# Revit family: IS_Connect_E8103_BIM_DE
name_source: partatom
category: Plumbing Fixtures
revit_build: Autodesk Revit MEP 2016 (Build: 20161004_0715(x64)
units: mm (PartAtom-declared; Revit-internal decimal feet)

## family parameters
Cut with Voids When Loaded = No
Host = Face
OmniClass Number = 23.45.05.14.14
OmniClass Title = Sinks/Lavatories
Part Type = Normal
Room Calculation Point = No
Round Connector Dimension = Use Diameter
Shared = No

## types (2) — shared parameters
Accessories = www.idealstandard.de\ersatzteile
AreaUnits = millimeters
AssetType = Fixed
BIMobject category = Basins
Brand url = http://www.idealstandard.co.uk
CodePerformance = DIN EN 14688 CL 00, DIN EN 31
Color = White
ConnectionType = Plumbing
CurrencyUnit = €
Date of publishing = 5/15/2017
Default Elevation = 850 mm
Description = Connect Lavabo 600 mm sans trop-plein
Dimensions = 460 x 600 x 174 mm
DurationUnit = year
Edition number = 1
ExpectedLife = 25
Features = CONNECT CUBE washbasin 600x460mm, 1 taphole, no overflow
Finish = White
GrossWeight = 17,502 kg
IFC Classification = Sanitary Terminal
IfcExportAs = IfcSanitaryTerminalType
IfcExportType = WASHHANDBASINS
Installation instructions = http://www.idealstandard.de
InstallationDate = 1900-12-31T23:59:59
InstallationInstructions = www.idealstandard.de\produkte
LinearUnits = millimeters
Manufacturer name = Ideal Standard
ManufacturerURL = www.idealstandard.de
Material = Vitreous china
Material main = Ceramics
NBS Reference Code = 31-79
NBS Reference Description = Sinks, Wash Basins And Troughs
Nominal height = 155 mm
Nominal width = 600 mm
NominalLength = 460 mm
OmniClass Code = 23-31 13 00
OmniClass Description = Sinks
Product Guid = 6d210ad9-f467-48dd-92bc-6a249ef587d0
Product SKU = E8103
Product data url = https://bimobject.com
Product family = CONNECT
Product group = Basin
Product url = http://www.idealstandard.de
ProductInformation = www.idealstandard.de
QR code = http://bimobject.com
Shape = Sculptured
Size = 600 x 460 x 174 mm
Space = Internal
Technical description = http://www.idealstandard.de
URL = www.idealstandard.de
Uniclass 1.4 Code = L7212
Uniclass 1.4 Description = Washbasins
Uniclass 2.0 Code = PR-31-79
Uniclass 2.0 Description = Sinks, Wash Basins And Troughs
Uniclass 2015 Code = Pr_40_20_96
Uniclass 2015 Name = Wash basins, sinks and troughs
Uniclass2015Code = Pr_40_20_96_96
Uniclass2015Title = Wall-hung wash basins
Uniclass2015Version = Products v1.1
Version = 1
VolumeUnits = Litres
Weight Net (Kg) = 17.5
zero-valued in all types: Cost, NominalDepth

## per-type parameters (varying)
| type | BarCode | EAN code | Model | ModelNumber | ModelReference |
| E810301 - CONNECT CUBE washbasin 600x460mm, 1 taphole, no overflow | 5017830403814 | https://5017830403814 | E810301 | E810301 | IS Waschtisch CONNECT CUBE, 1Hl., o.Ül., 600x460x175mm, Weiß |
| E8103MA - CONNECT CUBE washbasin 600x460mm, 1 taphole, no overflow | 5017830403807 | https://5017830403807 | E8103MA | E8103MA | IS Waschtisch CONNECT CUBE, 1Hl., o.Ül., 600x460x175mm, Weiß mit Ideal Plus |

## geometry (parser evidence)
native form markers: Blend x2, Sweep x3
no freeform markers — native parametric forms only
